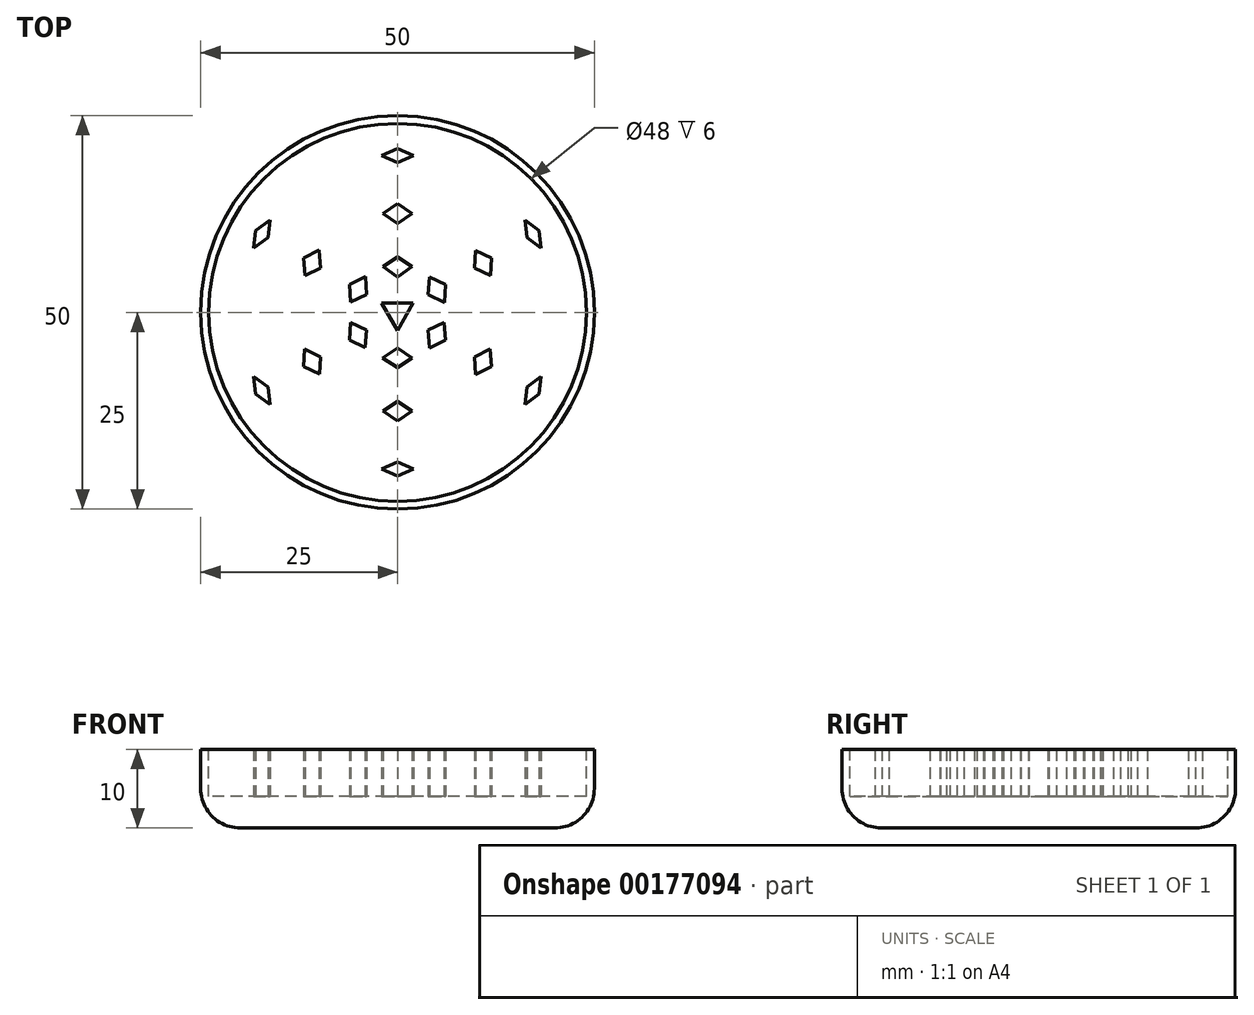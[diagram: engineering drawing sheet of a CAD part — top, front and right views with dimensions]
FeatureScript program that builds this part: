
annotation { "Feature Type Name" : "Feature", "Feature Type Description" : "" }
export const myFeature = defineFeature(function(context is Context, id is Id, definition is map)
    precondition{}
    {
        {
            var Q0;
            Q0=qCreatedBy(makeId("Top.planeOp"),FACE);
            var sketch = newSketch(context, id + "F0", { "sketchPlane" : qUnion([Q0])});
            skCircle(sketch, "E0", {"center": v(0, 0) * mm, "radius": 25 * mm});
            skSolve(sketch);
        }
        {
            var Q0;
            Q0=makeQuery(id+"F0.imprint","IMPRINT",FACE,{"disambiguationData":[TD([[makeQuery(id+"F0.imprint","IMPRINT",EDGE,{"derivedFrom":sQuery(id+"F0.wireOp",EDGE,"E0")}),1.0]])]});
            extrude(context, id + "F1", {"entities" : qUnion([Q0]), "depth" : 10 * mm});
        }
        {
            var Q0;
            Q0=makeQuery(id+"F1.opExtrude","CAP_FACE",FACE,{"disambiguationData":[OSD([sQuery(id+"F0.wireOp",EDGE,"E0")])],"isStart":false});
            var sketch = newSketch(context, id + "F2", { "sketchPlane" : qUnion([Q0])});
            skCircle(sketch, "E1", {"center": v(0, 0) * mm, "radius": 24 * mm});
            skSolve(sketch);
        }
        {
            var Q0;
            Q0=makeQuery(id+"F2.imprint","IMPRINT",FACE,{"disambiguationData":[TD([[makeQuery(id+"F2.imprint","IMPRINT",EDGE,{"derivedFrom":sQuery(id+"F2.wireOp",EDGE,"E1")}),1.0]])]});
            extrude(context, id + "F3", {"entities" : qUnion([Q0]), "operationType" : NewBodyOperationType.REMOVE, "oppositeDirection" : true, "depth" : 6 * mm});
        }
        {
            var Q0;
            Q0=makeQuery(id+"F3.boolean.opBoolean","COPY",FACE,{"derivedFrom":makeQuery(id+"F3.opExtrude","CAP_FACE",FACE,{"disambiguationData":[OSD([sQuery(id+"F2.wireOp",EDGE,"E1")])],"isStart":false})});
            var sketch = newSketch(context, id + "F4", { "sketchPlane" : qUnion([Q0])});
            skCircle(sketch, "E2.cCircle", {"center": v(0, 0) * mm, "radius": 1.15 * mm, "construction": true});
            skLineSegment(sketch, "E2.0", {"start": v(-2, 1.15) * mm, "end": v(2, 1.15) * mm});
            skLineSegment(sketch, "E2.1", {"start": v(2, 1.15) * mm, "end": v(0, -2.3) * mm});
            skLineSegment(sketch, "E2.2", {"start": v(0, -2.3) * mm, "end": v(-2, 1.15) * mm});
            skPoint(sketch, "E2.0.midPoint", {"position": v(0, 1.15) * mm});
            skSolve(sketch);
        }
        {
            var Q0;
            Q0=makeQuery(id+"F4.imprint","IMPRINT",FACE,{"disambiguationData":[TD([[makeQuery(id+"F4.imprint","IMPRINT",EDGE,{"derivedFrom":sQuery(id+"F4.wireOp",EDGE,"E2.0")}),-1.0]])]});
            extrude(context, id + "F5", {"entities" : qUnion([Q0]), "operationType" : NewBodyOperationType.ADD, "depth" : 6 * mm});
        }
        {
            var Q0;
            Q0=makeQuery(id+"F3.boolean.opBoolean","COPY",FACE,{"derivedFrom":makeQuery(id+"F3.opExtrude","CAP_FACE",FACE,{"disambiguationData":[OSD([sQuery(id+"F2.wireOp",EDGE,"E1")])],"isStart":false})});
            var sketch = newSketch(context, id + "F6", { "sketchPlane" : qUnion([Q0])});
            skLineSegment(sketch, "E3", {"start": v(2.06, 19.9) * mm, "end": v(0, 19) * mm});
            skLineSegment(sketch, "E4", {"start": v(0, 19) * mm, "end": v(-2.06, 19.9) * mm});
            skLineSegment(sketch, "E5", {"start": v(-2.06, 19.9) * mm, "end": v(0, 20.79) * mm});
            skLineSegment(sketch, "E6", {"start": v(0, 20.79) * mm, "end": v(2.06, 19.9) * mm});
            skLineSegment(sketch, "E7.1.0", {"start": v(-16.2, 11.73) * mm, "end": v(-16.45, 9.5) * mm});
            skLineSegment(sketch, "E7.1.1", {"start": v(-18.26, 8.17) * mm, "end": v(-18, 10.4) * mm});
            skLineSegment(sketch, "E7.1.2", {"start": v(-16.45, 9.5) * mm, "end": v(-18.26, 8.17) * mm});
            skLineSegment(sketch, "E7.1.3", {"start": v(-18, 10.4) * mm, "end": v(-16.2, 11.73) * mm});
            skLineSegment(sketch, "E7.2.0", {"start": v(-18.26, -8.17) * mm, "end": v(-16.45, -9.5) * mm});
            skLineSegment(sketch, "E7.2.1", {"start": v(-16.2, -11.73) * mm, "end": v(-18, -10.4) * mm});
            skLineSegment(sketch, "E7.2.2", {"start": v(-16.45, -9.5) * mm, "end": v(-16.2, -11.73) * mm});
            skLineSegment(sketch, "E7.2.3", {"start": v(-18, -10.4) * mm, "end": v(-18.26, -8.17) * mm});
            skLineSegment(sketch, "E7.3.0", {"start": v(-2.06, -19.9) * mm, "end": v(0, -19) * mm});
            skLineSegment(sketch, "E7.3.1", {"start": v(2.06, -19.9) * mm, "end": v(0, -20.79) * mm});
            skLineSegment(sketch, "E7.3.2", {"start": v(0, -19) * mm, "end": v(2.06, -19.9) * mm});
            skLineSegment(sketch, "E7.3.3", {"start": v(0, -20.79) * mm, "end": v(-2.06, -19.9) * mm});
            skLineSegment(sketch, "E7.4.0", {"start": v(16.2, -11.73) * mm, "end": v(16.45, -9.5) * mm});
            skLineSegment(sketch, "E7.4.1", {"start": v(18.26, -8.17) * mm, "end": v(18, -10.4) * mm});
            skLineSegment(sketch, "E7.4.2", {"start": v(16.45, -9.5) * mm, "end": v(18.26, -8.17) * mm});
            skLineSegment(sketch, "E7.4.3", {"start": v(18, -10.4) * mm, "end": v(16.2, -11.73) * mm});
            skLineSegment(sketch, "E7.5.0", {"start": v(18.26, 8.17) * mm, "end": v(16.45, 9.5) * mm});
            skLineSegment(sketch, "E7.5.1", {"start": v(16.2, 11.73) * mm, "end": v(18, 10.4) * mm});
            skLineSegment(sketch, "E7.5.2", {"start": v(16.45, 9.5) * mm, "end": v(16.2, 11.73) * mm});
            skLineSegment(sketch, "E7.5.3", {"start": v(18, 10.4) * mm, "end": v(18.26, 8.17) * mm});
            skPoint(sketch, "E7.center", {"position": v(0, 0) * mm});
            skSolve(sketch);
        }
        {
            var Q0;
            Q0=makeQuery(id+"F6.imprint","IMPRINT",FACE,{"disambiguationData":[TD([[makeQuery(id+"F6.imprint","IMPRINT",EDGE,{"derivedFrom":sQuery(id+"F6.wireOp",EDGE,"E3")}),-1.0]])]});
            var Q1;
            Q1=makeQuery(id+"F6.imprint","IMPRINT",FACE,{"disambiguationData":[TD([[makeQuery(id+"F6.imprint","IMPRINT",EDGE,{"derivedFrom":sQuery(id+"F6.wireOp",EDGE,"E7.5.0")}),-1.0]])]});
            var Q2;
            Q2=makeQuery(id+"F6.imprint","IMPRINT",FACE,{"disambiguationData":[TD([[makeQuery(id+"F6.imprint","IMPRINT",EDGE,{"derivedFrom":sQuery(id+"F6.wireOp",EDGE,"E7.4.0")}),-1.0]])]});
            var Q3;
            Q3=makeQuery(id+"F6.imprint","IMPRINT",FACE,{"disambiguationData":[TD([[makeQuery(id+"F6.imprint","IMPRINT",EDGE,{"derivedFrom":sQuery(id+"F6.wireOp",EDGE,"E7.3.0")}),-1.0]])]});
            var Q4;
            Q4=makeQuery(id+"F6.imprint","IMPRINT",FACE,{"disambiguationData":[TD([[makeQuery(id+"F6.imprint","IMPRINT",EDGE,{"derivedFrom":sQuery(id+"F6.wireOp",EDGE,"E7.2.0")}),-1.0]])]});
            var Q5;
            Q5=makeQuery(id+"F6.imprint","IMPRINT",FACE,{"disambiguationData":[TD([[makeQuery(id+"F6.imprint","IMPRINT",EDGE,{"derivedFrom":sQuery(id+"F6.wireOp",EDGE,"E7.1.0")}),-1.0]])]});
            extrude(context, id + "F7", {"entities" : qUnion([Q0, Q1, Q2, Q3, Q4, Q5]), "operationType" : NewBodyOperationType.ADD, "depth" : 6 * mm});
        }
        {
            var Q0;
            Q0=makeQuery(id+"F3.boolean.opBoolean","COPY",FACE,{"derivedFrom":makeQuery(id+"F3.opExtrude","CAP_FACE",FACE,{"disambiguationData":[OSD([sQuery(id+"F2.wireOp",EDGE,"E1")])],"isStart":false})});
            var sketch = newSketch(context, id + "F8", { "sketchPlane" : qUnion([Q0])});
            skLineSegment(sketch, "E8", {"start": v(1.86, 12.54) * mm, "end": v(0, 13.8) * mm});
            skLineSegment(sketch, "E9", {"start": v(0, 13.8) * mm, "end": v(-1.84, 12.52) * mm});
            skLineSegment(sketch, "E10", {"start": v(-1.84, 12.52) * mm, "end": v(0, 11.3) * mm});
            skLineSegment(sketch, "E11", {"start": v(0, 11.3) * mm, "end": v(1.86, 12.54) * mm});
            skLineSegment(sketch, "E12", {"start": v(0, 7.02) * mm, "end": v(-1.84, 5.8) * mm});
            skLineSegment(sketch, "E13", {"start": v(-1.84, 5.8) * mm, "end": v(0, 4.52) * mm});
            skLineSegment(sketch, "E14", {"start": v(0, 4.52) * mm, "end": v(1.88, 5.8) * mm});
            skLineSegment(sketch, "E15", {"start": v(1.88, 5.8) * mm, "end": v(0, 7.02) * mm});
            skLineSegment(sketch, "E16.1.0", {"start": v(-11.76, 4.66) * mm, "end": v(-9.78, 5.65) * mm});
            skLineSegment(sketch, "E16.1.1", {"start": v(-11.95, 6.9) * mm, "end": v(-11.76, 4.66) * mm});
            skLineSegment(sketch, "E16.1.2", {"start": v(-9.93, 7.88) * mm, "end": v(-11.95, 6.9) * mm});
            skLineSegment(sketch, "E16.1.3", {"start": v(-9.78, 5.65) * mm, "end": v(-9.93, 7.88) * mm});
            skLineSegment(sketch, "E16.1.4", {"start": v(-5.94, 1.3) * mm, "end": v(-3.91, 2.26) * mm});
            skLineSegment(sketch, "E16.1.5", {"start": v(-3.91, 2.26) * mm, "end": v(-4.08, 4.52) * mm});
            skLineSegment(sketch, "E16.1.6", {"start": v(-6.08, 3.5) * mm, "end": v(-5.94, 1.3) * mm});
            skLineSegment(sketch, "E16.1.7", {"start": v(-4.08, 4.52) * mm, "end": v(-6.08, 3.5) * mm});
            skLineSegment(sketch, "E16.2.0", {"start": v(-9.92, -7.85) * mm, "end": v(-9.78, -5.65) * mm});
            skLineSegment(sketch, "E16.2.1", {"start": v(-11.95, -6.9) * mm, "end": v(-9.92, -7.85) * mm});
            skLineSegment(sketch, "E16.2.2", {"start": v(-11.8, -4.66) * mm, "end": v(-11.95, -6.9) * mm});
            skLineSegment(sketch, "E16.2.3", {"start": v(-9.78, -5.65) * mm, "end": v(-11.8, -4.66) * mm});
            skLineSegment(sketch, "E16.2.4", {"start": v(-4.1, -4.5) * mm, "end": v(-3.91, -2.26) * mm});
            skLineSegment(sketch, "E16.2.5", {"start": v(-3.91, -2.26) * mm, "end": v(-5.96, -1.27) * mm});
            skLineSegment(sketch, "E16.2.6", {"start": v(-6.08, -3.5) * mm, "end": v(-4.1, -4.5) * mm});
            skLineSegment(sketch, "E16.2.7", {"start": v(-5.96, -1.27) * mm, "end": v(-6.08, -3.5) * mm});
            skLineSegment(sketch, "E16.3.0", {"start": v(1.84, -12.52) * mm, "end": v(0, -11.3) * mm});
            skLineSegment(sketch, "E16.3.1", {"start": v(0, -13.8) * mm, "end": v(1.84, -12.52) * mm});
            skLineSegment(sketch, "E16.3.2", {"start": v(-1.86, -12.54) * mm, "end": v(0, -13.8) * mm});
            skLineSegment(sketch, "E16.3.3", {"start": v(0, -11.3) * mm, "end": v(-1.86, -12.54) * mm});
            skLineSegment(sketch, "E16.3.4", {"start": v(1.84, -5.8) * mm, "end": v(0, -4.52) * mm});
            skLineSegment(sketch, "E16.3.5", {"start": v(0, -4.52) * mm, "end": v(-1.88, -5.8) * mm});
            skLineSegment(sketch, "E16.3.6", {"start": v(0, -7.02) * mm, "end": v(1.84, -5.8) * mm});
            skLineSegment(sketch, "E16.3.7", {"start": v(-1.88, -5.8) * mm, "end": v(0, -7.02) * mm});
            skLineSegment(sketch, "E16.4.0", {"start": v(11.76, -4.66) * mm, "end": v(9.78, -5.65) * mm});
            skLineSegment(sketch, "E16.4.1", {"start": v(11.95, -6.9) * mm, "end": v(11.76, -4.66) * mm});
            skLineSegment(sketch, "E16.4.2", {"start": v(9.93, -7.88) * mm, "end": v(11.95, -6.9) * mm});
            skLineSegment(sketch, "E16.4.3", {"start": v(9.78, -5.65) * mm, "end": v(9.93, -7.88) * mm});
            skLineSegment(sketch, "E16.4.4", {"start": v(5.94, -1.3) * mm, "end": v(3.91, -2.26) * mm});
            skLineSegment(sketch, "E16.4.5", {"start": v(3.91, -2.26) * mm, "end": v(4.08, -4.52) * mm});
            skLineSegment(sketch, "E16.4.6", {"start": v(6.08, -3.5) * mm, "end": v(5.94, -1.3) * mm});
            skLineSegment(sketch, "E16.4.7", {"start": v(4.08, -4.52) * mm, "end": v(6.08, -3.5) * mm});
            skLineSegment(sketch, "E16.5.0", {"start": v(9.92, 7.85) * mm, "end": v(9.78, 5.65) * mm});
            skLineSegment(sketch, "E16.5.1", {"start": v(11.95, 6.9) * mm, "end": v(9.92, 7.85) * mm});
            skLineSegment(sketch, "E16.5.2", {"start": v(11.8, 4.66) * mm, "end": v(11.95, 6.9) * mm});
            skLineSegment(sketch, "E16.5.3", {"start": v(9.78, 5.65) * mm, "end": v(11.8, 4.66) * mm});
            skLineSegment(sketch, "E16.5.4", {"start": v(4.1, 4.5) * mm, "end": v(3.91, 2.26) * mm});
            skLineSegment(sketch, "E16.5.5", {"start": v(3.91, 2.26) * mm, "end": v(5.96, 1.27) * mm});
            skLineSegment(sketch, "E16.5.6", {"start": v(6.08, 3.5) * mm, "end": v(4.1, 4.5) * mm});
            skLineSegment(sketch, "E16.5.7", {"start": v(5.96, 1.27) * mm, "end": v(6.08, 3.5) * mm});
            skPoint(sketch, "E16.center", {"position": v(0, 0) * mm});
            skSolve(sketch);
        }
        {
            var Q0;
            Q0=makeQuery(id+"F8.imprint","IMPRINT",FACE,{"disambiguationData":[TD([[makeQuery(id+"F8.imprint","IMPRINT",EDGE,{"derivedFrom":sQuery(id+"F8.wireOp",EDGE,"E16.3.0")}),1.0]])]});
            var Q1;
            Q1=makeQuery(id+"F8.imprint","IMPRINT",FACE,{"disambiguationData":[TD([[makeQuery(id+"F8.imprint","IMPRINT",EDGE,{"derivedFrom":sQuery(id+"F8.wireOp",EDGE,"E16.3.4")}),1.0]])]});
            var Q2;
            Q2=makeQuery(id+"F8.imprint","IMPRINT",FACE,{"disambiguationData":[TD([[makeQuery(id+"F8.imprint","IMPRINT",EDGE,{"derivedFrom":sQuery(id+"F8.wireOp",EDGE,"E16.4.4")}),1.0]])]});
            var Q3;
            Q3=makeQuery(id+"F8.imprint","IMPRINT",FACE,{"disambiguationData":[TD([[makeQuery(id+"F8.imprint","IMPRINT",EDGE,{"derivedFrom":sQuery(id+"F8.wireOp",EDGE,"E16.4.0")}),1.0]])]});
            var Q4;
            Q4=makeQuery(id+"F8.imprint","IMPRINT",FACE,{"disambiguationData":[TD([[makeQuery(id+"F8.imprint","IMPRINT",EDGE,{"derivedFrom":sQuery(id+"F8.wireOp",EDGE,"E16.5.4")}),1.0]])]});
            var Q5;
            Q5=makeQuery(id+"F8.imprint","IMPRINT",FACE,{"disambiguationData":[TD([[makeQuery(id+"F8.imprint","IMPRINT",EDGE,{"derivedFrom":sQuery(id+"F8.wireOp",EDGE,"E12")}),1.0]])]});
            var Q6;
            Q6=makeQuery(id+"F8.imprint","IMPRINT",FACE,{"disambiguationData":[TD([[makeQuery(id+"F8.imprint","IMPRINT",EDGE,{"derivedFrom":sQuery(id+"F8.wireOp",EDGE,"E16.1.4")}),1.0]])]});
            var Q7;
            Q7=makeQuery(id+"F8.imprint","IMPRINT",FACE,{"disambiguationData":[TD([[makeQuery(id+"F8.imprint","IMPRINT",EDGE,{"derivedFrom":sQuery(id+"F8.wireOp",EDGE,"E16.2.4")}),1.0]])]});
            var Q8;
            Q8=makeQuery(id+"F8.imprint","IMPRINT",FACE,{"disambiguationData":[TD([[makeQuery(id+"F8.imprint","IMPRINT",EDGE,{"derivedFrom":sQuery(id+"F8.wireOp",EDGE,"E16.2.0")}),1.0]])]});
            var Q9;
            Q9=makeQuery(id+"F8.imprint","IMPRINT",FACE,{"disambiguationData":[TD([[makeQuery(id+"F8.imprint","IMPRINT",EDGE,{"derivedFrom":sQuery(id+"F8.wireOp",EDGE,"E16.1.0")}),1.0]])]});
            var Q10;
            Q10=makeQuery(id+"F8.imprint","IMPRINT",FACE,{"disambiguationData":[TD([[makeQuery(id+"F8.imprint","IMPRINT",EDGE,{"derivedFrom":sQuery(id+"F8.wireOp",EDGE,"E8")}),1.0]])]});
            var Q11;
            Q11=makeQuery(id+"F8.imprint","IMPRINT",FACE,{"disambiguationData":[TD([[makeQuery(id+"F8.imprint","IMPRINT",EDGE,{"derivedFrom":sQuery(id+"F8.wireOp",EDGE,"E16.5.0")}),1.0]])]});
            extrude(context, id + "F9", {"entities" : qUnion([Q0, Q1, Q2, Q3, Q4, Q5, Q6, Q7, Q8, Q9, Q10, Q11]), "operationType" : NewBodyOperationType.ADD, "depth" : 6 * mm});
        }
        {
            var Q0;
            Q0=makeQuery(id+"F1.opExtrude","CAP_EDGE",EDGE,{"disambiguationData":[OSD([sQuery(id+"F0.wireOp",EDGE,"E0")])],"isStart":true});
            fillet(context, id + "F10", {"entities" : qUnion([Q0]), "radius" : 5 * mm, "tangentPropagation" : true, "allowEdgeOverflow" : false});
        }
    });
